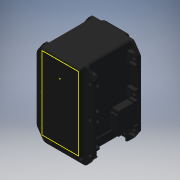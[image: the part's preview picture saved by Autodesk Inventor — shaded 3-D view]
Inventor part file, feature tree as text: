
AUTODESK INVENTOR PART (.ipt)
format: ipt  version: 2016 (Build 200138000, 138)  size: 652,288 bytes
history: native  units: in
note: dims shown in document units (in); Inventor stores cm internally (conversion verified against a paired STEP export)
features: sketch x3, other x1, extrude x1, imported_body x1
ambient origin geometry x8: Origin, YZ Plane, XZ Plane, XY Plane, X Axis, Y Axis, Z Axis, Center Point
bodies: Solid1 (feature_tree)
feature tree (6):
  other  "MX-64T1"
  sketch  "Sketch1"  dims[d2=0.1575in d3=0.0in d4=0.0in]
  sketch  "Sketch2"
  extrude  "Extrusion1"  Depth=0.0in TaperAngle=0.0deg
  imported_body  "Base1"
  sketch  "Sketch3"
